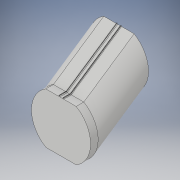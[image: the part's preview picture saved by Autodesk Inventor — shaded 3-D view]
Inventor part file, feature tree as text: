
AUTODESK INVENTOR PART (.ipt)
format: ipt  version: 2017 (Build 210142000, 142)  size: 178,176 bytes
history: native  units: in
note: dims shown in document units (in); Inventor stores cm internally (conversion verified against a paired STEP export)
features: sketch x2, plane x1, sweep x1, extrude x1
ambient origin geometry x8: Origin, YZ Plane, XZ Plane, XY Plane, X Axis, Y Axis, Z Axis, Center Point
bodies: Solid1 (feature_tree)
feature tree (5):
  sketch  "Sketch1"  dims[d0=6.6667in d28=8.0in]
  plane  "Work Plane2"
  sweep  "ramp"
  extrude  "connection bottom"  Depth=0.0884in TaperAngle=0.0deg
  sketch  "Sketch6"  dims[d30=0.0in d31=0.0in d32=1.0in d33=0.0in d62=0.8521in d110=4.0in d111=0.5833in d112=3.8873in d113=3.8873in d114=1.7083in d115=0.0625in d116=0.0625in d117=1.6458in d118=0.25in d119=0.125in d121=0.0884in d122=45.0deg d123=3.3333in d124=0.125in d125=4.0in d126=0.5833in d127=3.8873in d128=3.8873in d129=1.7083in d130=0.0625in d131=0.0625in d132=1.6458in d133=0.25in d134=0.125in d136=0.0884in d137=45.0deg d138=3.3333in d139=0.125in]
